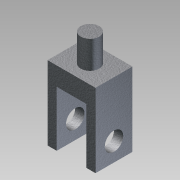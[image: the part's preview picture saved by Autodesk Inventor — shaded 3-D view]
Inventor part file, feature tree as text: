
AUTODESK INVENTOR PART (.ipt)
format: ipt  version: 2013 (Build 170138000, 138)  size: 112,640 bytes
history: native  units: in
note: dims shown in document units (in); Inventor stores cm internally (conversion verified against a paired STEP export)
features: extrude x3, sketch x3
ambient origin geometry x8: Origin, YZ Plane, XZ Plane, XY Plane, X Axis, Y Axis, Z Axis, Center Point
bodies: Solid1 (feature_tree)
feature tree (6):
  extrude  "Extrusion1"  Depth=2.0in
  extrude  "Extrusion2"  Depth=0.25in
  extrude  "Extrusion3"  Depth=1.0in TaperAngle=0.0deg
  sketch  "Sketch1"  dims[d0=1.3in d1=2.0in]
  sketch  "Sketch2"  dims[d2=0.25in d3=0.25in]
  sketch  "Sketch3"  dims[d4=0.25in d5=1.0in d6=0.0in d7=0.5in d8=0.5in d9=10.0in d10=0.0in d11=2.0in d12=0.5in d13=0.75in d14=0.0in d15=1.5in]
